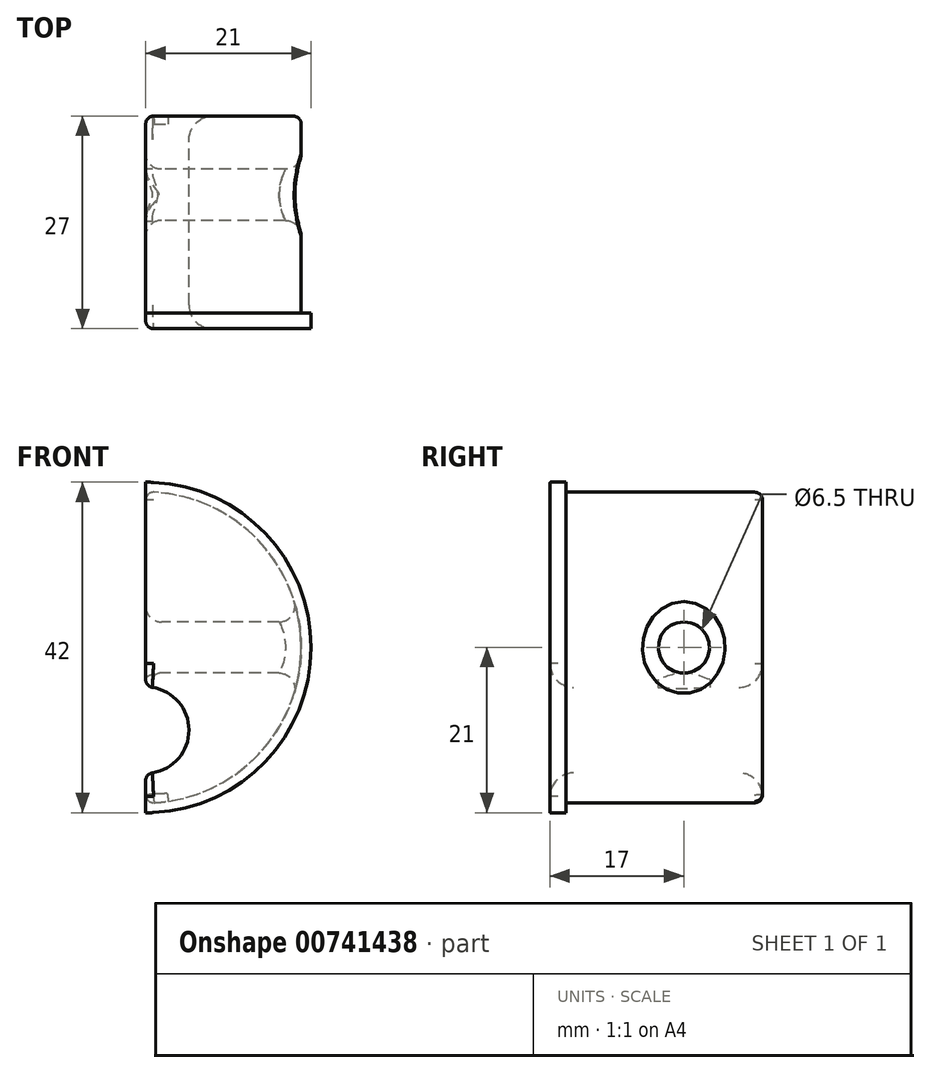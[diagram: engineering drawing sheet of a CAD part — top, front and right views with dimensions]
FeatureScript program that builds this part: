
annotation { "Feature Type Name" : "Feature", "Feature Type Description" : "" }
export const myFeature = defineFeature(function(context is Context, id is Id, definition is map)
    precondition{}
    {
        {
            var Q0;
            Q0=qCreatedBy(makeId("Front.planeOp"),FACE);
            var sketch = newSketch(context, id + "F0", { "sketchPlane" : qUnion([Q0])});
            skCircle(sketch, "E0", {"center": v(0, 0) * mm, "radius": 21 * mm});
            skCircle(sketch, "E1", {"center": v(0, 0) * mm, "radius": 19.75 * mm});
            skCircle(sketch, "E2", {"center": v(0, -10.5) * mm, "radius": 5.5 * mm});
            skSolve(sketch);
        }
        {
            var Q0;
            Q0=makeQuery(id+"F0.imprint","IMPRINT",FACE,{"disambiguationData":[TD([[makeQuery(id+"F0.imprint","IMPRINT",EDGE,{"derivedFrom":sQuery(id+"F0.wireOp",EDGE,"E1")}),1.0]])]});
            extrude(context, id + "F1", {"entities" : qUnion([Q0]), "depth" : 25 * mm, "offsetDistance" : 25 * mm});
        }
        {
            var Q0;
            Q0=makeQuery(id+"F1.opExtrude","CAP_FACE",FACE,{"disambiguationData":[OSD([sQuery(id+"F0.wireOp",EDGE,"E1"),sQuery(id+"F0.wireOp",EDGE,"E2")])],"isStart":false});
            var sketch = newSketch(context, id + "F2", { "sketchPlane" : qUnion([Q0])});
            skCircle(sketch, "E3", {"center": v(0, 0) * mm, "radius": 21 * mm});
            skSolve(sketch);
        }
        {
            var Q0;
            Q0=makeQuery(id+"F2.imprint","IMPRINT",FACE,{"disambiguationData":[TD([[makeQuery(id+"F2.imprint","IMPRINT",EDGE,{"derivedFrom":sQuery(id+"F2.wireOp",EDGE,"E3")}),1.0]])]});
            var Q1;
            Q1=makeQuery(id+"F2.imprint","IMPRINT",FACE,{"disambiguationData":[TD([[makeQuery(id+"F2.imprint","IMPRINT",EDGE,{"derivedFrom":makeQuery(id+"F1.opExtrude","CAP_EDGE",EDGE,{"disambiguationData":[OSD([sQuery(id+"F0.wireOp",EDGE,"E1")])],"isStart":false})}),1.0]])]});
            extrude(context, id + "F3", {"entities" : qUnion([Q0, Q1]), "operationType" : NewBodyOperationType.ADD, "depth" : 2 * mm, "offsetDistance" : 25 * mm});
        }
        {
            var Q0;
            Q0=qCreatedBy(makeId("Right.planeOp"),FACE);
            var sketch = newSketch(context, id + "F4", { "sketchPlane" : qUnion([Q0])});
            skCircle(sketch, "E4", {"center": v(-10, 0) * mm, "radius": 3.25 * mm});
            skSolve(sketch);
        }
        {
            var Q0;
            Q0=makeQuery(id+"F4.imprint","IMPRINT",FACE,{"disambiguationData":[TD([[makeQuery(id+"F4.imprint","IMPRINT",EDGE,{"derivedFrom":sQuery(id+"F4.wireOp",EDGE,"E4")}),1.0]])]});
            extrude(context, id + "F5", {"entities" : qUnion([Q0]), "operationType" : NewBodyOperationType.REMOVE, "endBound" : BoundingType.SYMMETRIC, "depth" : 50 * mm, "offsetDistance" : 25 * mm});
        }
        {
            var Q0;
            Q0=makeQuery(id+"F3.opExtrude","CAP_FACE",FACE,{"disambiguationData":[OSD([sQuery(id+"F0.wireOp",EDGE,"E2"),sQuery(id+"F2.wireOp",EDGE,"E3")])],"isStart":false});
            var sketch = newSketch(context, id + "F6", { "sketchPlane" : qUnion([Q0])});
            skLineSegment(sketch, "E5.bottom", {"start": v(-30, 22.87) * mm, "end": v(0, 22.87) * mm});
            skLineSegment(sketch, "E5.top", {"start": v(-30, -25.31) * mm, "end": v(0, -25.31) * mm});
            skLineSegment(sketch, "E5.left", {"start": v(0, 22.87) * mm, "end": v(0, -25.31) * mm});
            skLineSegment(sketch, "E5.right", {"start": v(-30, 22.87) * mm, "end": v(-30, -25.31) * mm});
            skSolve(sketch);
        }
        {
            var Q0;
            {var subQ0=sQuery(id+"F6.wireOp",EDGE,"E5.left");var subQ1=makeQuery(id+"F3.opExtrude","CAP_EDGE",EDGE,{"disambiguationData":[OSD([sQuery(id+"F2.wireOp",EDGE,"E3")])],"isStart":false});var subQ2=makeQuery(id+"F6.imprint","INTERSECT",VERTEX,{"disambiguationData":[OD(0.0)],"derivedFrom":[subQ1,subQ0]});Q0=makeQuery(id+"F6.imprint","IMPRINT",FACE,{"disambiguationData":[TD([[makeQuery(id+"F6.imprint","IMPRINT",EDGE,{"disambiguationData":[TD([[subQ2,-1.0]])],"derivedFrom":subQ0}),-1.0]])]});}
            var Q1;
            {var subQ1=sQuery(id+"F6.wireOp",EDGE,"E5.bottom");Q1=makeQuery(id+"F6.imprint","IMPRINT",FACE,{"disambiguationData":[TD([[makeQuery(id+"F6.imprint","IMPRINT",EDGE,{"derivedFrom":subQ1}),-1.0]])]});}
            extrude(context, id + "F7", {"entities" : qUnion([Q0, Q1]), "operationType" : NewBodyOperationType.REMOVE, "endBound" : BoundingType.THROUGH_ALL, "oppositeDirection" : true, "depth" : 25 * mm, "offsetDistance" : 25 * mm});
        }
        {
            var Q0;
            {var subQ0=sQuery(id+"F6.wireOp",EDGE,"E5.left");var subQ1=makeQuery(id+"F6.imprint","INTERSECT",VERTEX,{"disambiguationData":[OD(0.0)],"derivedFrom":[makeQuery(id+"F3.opExtrude","CAP_EDGE",EDGE,{"disambiguationData":[OSD([sQuery(id+"F2.wireOp",EDGE,"E3")])],"isStart":false}),subQ0]});Q0=makeQuery(id+"F7.boolean.opBoolean","INTERSECT",EDGE,{"derivedFrom":[makeQuery(id+"F5.boolean.opBoolean","COPY",FACE,{"derivedFrom":makeQuery(id+"F5.opExtrude","SWEPT_FACE",FACE,{"disambiguationData":[OSD([sQuery(id+"F4.wireOp",EDGE,"E4")])]})}),makeQuery(id+"F7.opExtrude","SWEPT_FACE",FACE,{"disambiguationData":[OSD([subQ0]),TDD([makeQuery(id+"F6.imprint","IMPRINT",EDGE,{"disambiguationData":[TD([[makeQuery(id+"F6.imprint","INTERSECT",VERTEX,{"derivedFrom":[sQuery(id+"F6.wireOp",EDGE,"E5.bottom"),subQ0]}),-1.0]])],"derivedFrom":subQ0}),makeQuery(id+"F6.imprint","IMPRINT",EDGE,{"disambiguationData":[TD([[subQ1,-1.0]])],"derivedFrom":subQ0})])]})]});}
            fillet(context, id + "F8", {"entities" : qUnion([Q0]), "radius" : 2 * mm, "tangentPropagation" : true, "allowEdgeOverflow" : false});
        }
        {
            var Q0;
            Q0=makeQuery(id+"F5.boolean.opBoolean","INTERSECT",EDGE,{"disambiguationData":[OD(0.0)],"derivedFrom":[makeQuery(id+"F1.opExtrude","SWEPT_FACE",FACE,{"disambiguationData":[OSD([sQuery(id+"F0.wireOp",EDGE,"E1")])]}),makeQuery(id+"F5.opExtrude","SWEPT_FACE",FACE,{"disambiguationData":[OSD([sQuery(id+"F4.wireOp",EDGE,"E4")])]})]});
            var Q1;
            Q1=makeQuery(id+"F5.boolean.opBoolean","INTERSECT",EDGE,{"disambiguationData":[OD(1.0)],"derivedFrom":[makeQuery(id+"F1.opExtrude","SWEPT_FACE",FACE,{"disambiguationData":[OSD([sQuery(id+"F0.wireOp",EDGE,"E1")])]}),makeQuery(id+"F5.opExtrude","SWEPT_FACE",FACE,{"disambiguationData":[OSD([sQuery(id+"F4.wireOp",EDGE,"E4")])]})]});
            fillet(context, id + "F9", {"entities" : qUnion([Q0, Q1]), "radius" : 2 * mm, "tangentPropagation" : true, "allowEdgeOverflow" : false});
        }
        {
            var Q0;
            Q0=makeQuery(id+"F3.opExtrude","CAP_EDGE",EDGE,{"disambiguationData":[OSD([sQuery(id+"F0.wireOp",EDGE,"E2")])],"isStart":false});
            var Q1;
            Q1=makeQuery(id+"F1.opExtrude","CAP_EDGE",EDGE,{"disambiguationData":[OSD([sQuery(id+"F0.wireOp",EDGE,"E2")])],"isStart":true});
            fillet(context, id + "F10", {"entities" : qUnion([Q0, Q1]), "radius" : 3 * mm, "tangentPropagation" : true, "allowEdgeOverflow" : false});
        }
        {
            var Q0;
            {var subQ0=sQuery(id+"F6.wireOp",EDGE,"E5.left");var subQ1=sQuery(id+"F0.wireOp",EDGE,"E2");Q0=makeQuery(id+"F7.boolean.opBoolean","COPY",EDGE,{"derivedFrom":makeQuery(id+"F7.opExtrude","SWEPT_EDGE",EDGE,{"disambiguationData":[OSD([subQ1,subQ0]),TDD([makeQuery(id+"F6.imprint","INTERSECT",VERTEX,{"disambiguationData":[OD(0.0)],"derivedFrom":[makeQuery(id+"F3.opExtrude","CAP_EDGE",EDGE,{"disambiguationData":[OSD([subQ1])],"isStart":false}),subQ0]})])]})});}
            var Q1;
            {var subQ0=sQuery(id+"F0.wireOp",EDGE,"E2");var subQ1=sQuery(id+"F6.wireOp",EDGE,"E5.left");var subQ2=makeQuery(id+"F6.imprint","INTERSECT",VERTEX,{"disambiguationData":[OD(0.0)],"derivedFrom":[makeQuery(id+"F3.opExtrude","CAP_EDGE",EDGE,{"disambiguationData":[OSD([sQuery(id+"F2.wireOp",EDGE,"E3")])],"isStart":false}),subQ1]});Q1=makeQuery(id+"F8.opFillet","BLEND_EDGE",EDGE,{"blendedFrom":[makeQuery(id+"F7.boolean.opBoolean","INTERSECT",EDGE,{"derivedFrom":[makeQuery(id+"F5.boolean.opBoolean","COPY",FACE,{"derivedFrom":makeQuery(id+"F5.opExtrude","SWEPT_FACE",FACE,{"disambiguationData":[OSD([sQuery(id+"F4.wireOp",EDGE,"E4")])]})}),makeQuery(id+"F7.opExtrude","SWEPT_FACE",FACE,{"disambiguationData":[OSD([subQ1]),TDD([makeQuery(id+"F6.imprint","IMPRINT",EDGE,{"disambiguationData":[TD([[makeQuery(id+"F6.imprint","INTERSECT",VERTEX,{"derivedFrom":[sQuery(id+"F6.wireOp",EDGE,"E5.bottom"),subQ1]}),-1.0]])],"derivedFrom":subQ1}),makeQuery(id+"F6.imprint","IMPRINT",EDGE,{"disambiguationData":[TD([[subQ2,-1.0]])],"derivedFrom":subQ1})])]})]}),makeQuery(id+"F3.boolean.opBoolean","MERGE",FACE,{"derivedFrom":[makeQuery(id+"F1.opExtrude","SWEPT_FACE",FACE,{"disambiguationData":[OSD([subQ0])]}),makeQuery(id+"F3.opExtrude","SWEPT_FACE",FACE,{"disambiguationData":[OSD([subQ0])]})]})],"blendedInto":[makeQuery(id+"F3.boolean.opBoolean","MERGE",FACE,{"derivedFrom":[makeQuery(id+"F1.opExtrude","SWEPT_FACE",FACE,{"disambiguationData":[OSD([subQ0])]}),makeQuery(id+"F3.opExtrude","SWEPT_FACE",FACE,{"disambiguationData":[OSD([subQ0])]})]})]});}
            var Q2;
            {var subQ0=sQuery(id+"F0.wireOp",EDGE,"E2");Q2=makeQuery(id+"F3.boolean.opBoolean","MERGE",FACE,{"derivedFrom":[makeQuery(id+"F1.opExtrude","SWEPT_FACE",FACE,{"disambiguationData":[OSD([subQ0])]}),makeQuery(id+"F3.opExtrude","SWEPT_FACE",FACE,{"disambiguationData":[OSD([subQ0])]})]});}
            fillet(context, id + "F11", {"entities" : qUnion([Q0, Q1, Q2]), "radius" : 1 * mm, "tangentPropagation" : true, "allowEdgeOverflow" : false});
        }
        {
            var Q0;
            Q0=makeQuery(id+"F1.opExtrude","CAP_EDGE",EDGE,{"disambiguationData":[OSD([sQuery(id+"F0.wireOp",EDGE,"E1")])],"isStart":true});
            var Q1;
            {var subQ0=sQuery(id+"F0.wireOp",EDGE,"E2");var subQ1=makeQuery(id+"F1.opExtrude","CAP_FACE",FACE,{"disambiguationData":[OSD([sQuery(id+"F0.wireOp",EDGE,"E1"),subQ0])],"isStart":true});var subQ2=sQuery(id+"F6.wireOp",EDGE,"E5.left");var subQ3=makeQuery(id+"F6.imprint","INTERSECT",VERTEX,{"disambiguationData":[OD(0.0)],"derivedFrom":[makeQuery(id+"F3.opExtrude","CAP_EDGE",EDGE,{"disambiguationData":[OSD([sQuery(id+"F2.wireOp",EDGE,"E3")])],"isStart":false}),subQ2]});Q1=makeQuery(id+"F11.opFillet","BLEND_EDGE",EDGE,{"blendedFrom":[makeQuery(id+"F7.boolean.opBoolean","INTERSECT",EDGE,{"derivedFrom":[subQ1,makeQuery(id+"F7.opExtrude","SWEPT_FACE",FACE,{"disambiguationData":[OSD([subQ2]),TDD([makeQuery(id+"F6.imprint","IMPRINT",EDGE,{"disambiguationData":[TD([[makeQuery(id+"F6.imprint","INTERSECT",VERTEX,{"derivedFrom":[sQuery(id+"F6.wireOp",EDGE,"E5.bottom"),subQ2]}),-1.0]])],"derivedFrom":subQ2}),makeQuery(id+"F6.imprint","IMPRINT",EDGE,{"disambiguationData":[TD([[subQ3,-1.0]])],"derivedFrom":subQ2})])]})]}),subQ1],"blendedInto":[subQ1]});}
            var Q2;
            {var subQ0=sQuery(id+"F0.wireOp",EDGE,"E2");var subQ1=makeQuery(id+"F1.opExtrude","CAP_FACE",FACE,{"disambiguationData":[OSD([sQuery(id+"F0.wireOp",EDGE,"E1"),subQ0])],"isStart":true});var subQ2=sQuery(id+"F6.wireOp",EDGE,"E5.left");var subQ3=makeQuery(id+"F6.imprint","INTERSECT",VERTEX,{"disambiguationData":[OD(1.0)],"derivedFrom":[makeQuery(id+"F3.opExtrude","CAP_EDGE",EDGE,{"disambiguationData":[OSD([sQuery(id+"F2.wireOp",EDGE,"E3")])],"isStart":false}),subQ2]});Q2=makeQuery(id+"F11.opFillet","BLEND_EDGE",EDGE,{"blendedFrom":[makeQuery(id+"F7.boolean.opBoolean","INTERSECT",EDGE,{"derivedFrom":[subQ1,makeQuery(id+"F7.opExtrude","SWEPT_FACE",FACE,{"disambiguationData":[OSD([subQ2]),TDD([makeQuery(id+"F6.imprint","IMPRINT",EDGE,{"disambiguationData":[TD([[subQ3,1.0]])],"derivedFrom":subQ2}),makeQuery(id+"F6.imprint","IMPRINT",EDGE,{"disambiguationData":[TD([[makeQuery(id+"F6.imprint","INTERSECT",VERTEX,{"derivedFrom":[sQuery(id+"F6.wireOp",EDGE,"E5.top"),subQ2]}),1.0]])],"derivedFrom":subQ2})])]})]}),subQ1],"blendedInto":[subQ1]});}
            fillet(context, id + "F12", {"entities" : qUnion([Q0, Q1, Q2]), "radius" : 1 * mm, "tangentPropagation" : true, "allowEdgeOverflow" : false});
        }
    });
